# Revit family: REVIT-MG-1048-SolnawithReceptacle-
name_source: partatom
category: Furniture
revit_build: Autodesk Revit 2016 (Build: 20150220_1215(x64)
units: mm (PartAtom-declared; Revit-internal decimal feet)

## family parameters
Always vertical = Yes
Cut with Voids When Loaded = No
OmniClass Number = 23.40.20.00
OmniClass Title = General Furniture and Specialties
Room Calculation Point = No
Shared = No
Work Plane-Based = No

## types (1)
- MG-1048
    Description = Solna with Receptacle
    Glide Finish = MAG - Plastic Black
    Lock Finish = MAG - Anodized Silver
    Low Emitting Finish = Yes
    Low Emitting Material = Yes
    Manufacturer = Magnuson Group
    Model = MG-1048
    Percentage of Recycled Content = 0
    Revit File Built By = https://servex-us.com
    SOLNA-ADD-18-MD = Yes
    Salvage or Reuse = Yes
    Type Comments = Stand Alone
    URL = www.magnusongroup.com

## geometry (parser evidence)
native form markers: Blend x2, Extrusion x1, Sweep x17
no freeform markers — native parametric forms only
